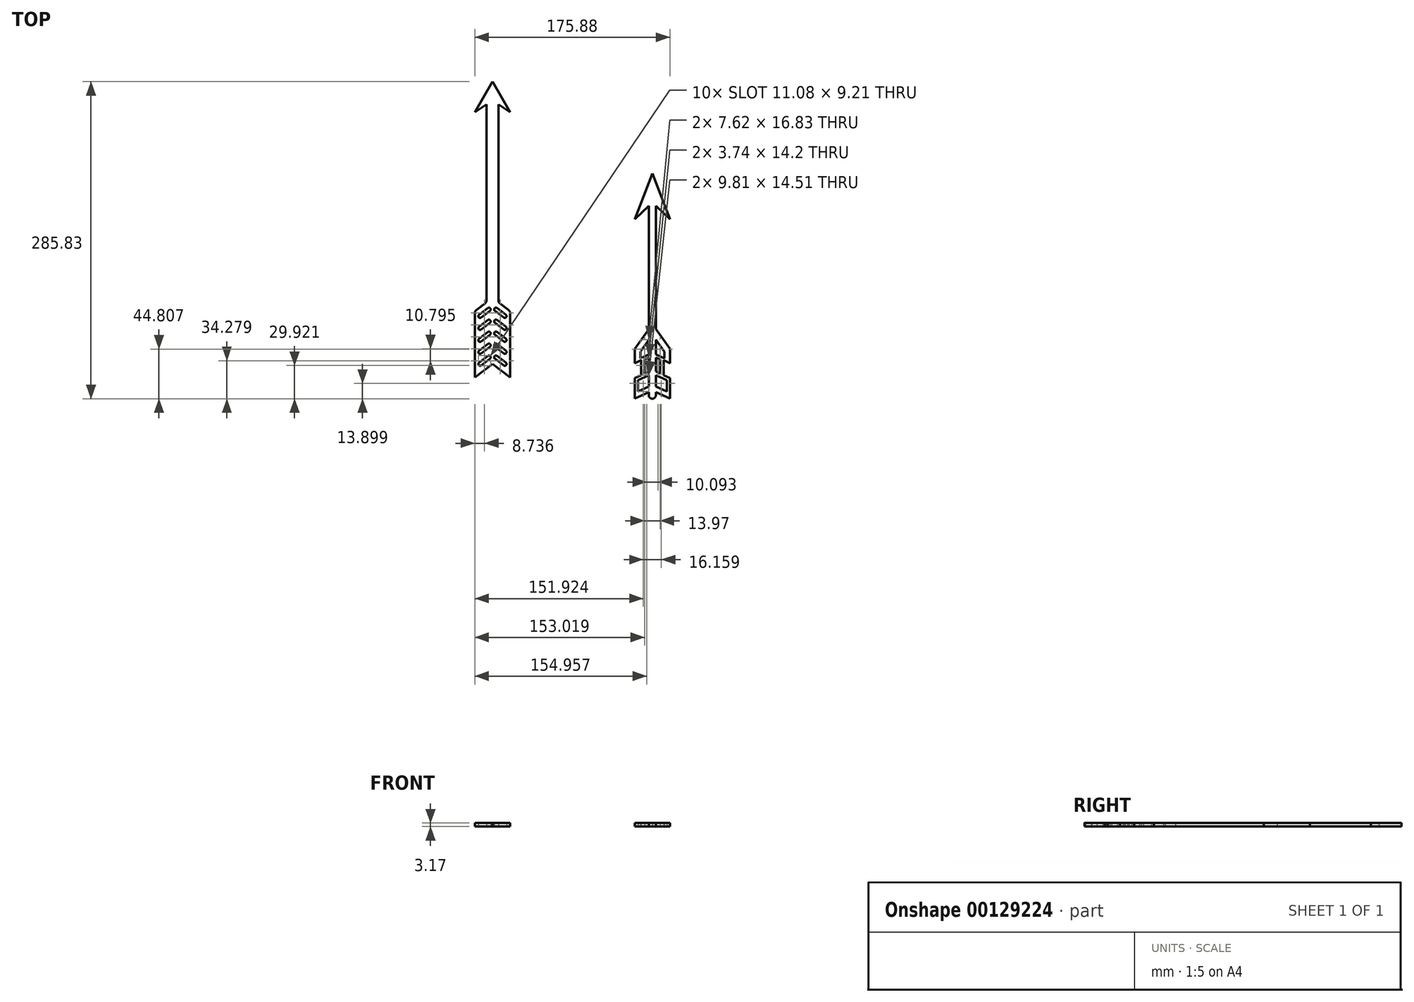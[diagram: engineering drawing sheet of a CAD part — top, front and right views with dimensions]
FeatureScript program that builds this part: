
annotation { "Feature Type Name" : "Feature", "Feature Type Description" : "" }
export const myFeature = defineFeature(function(context is Context, id is Id, definition is map)
    precondition{}
    {
        {
            var Q0;
            Q0=qCreatedBy(makeId("Top.planeOp"),FACE);
            var sketch = newSketch(context, id + "F0", { "sketchPlane" : qUnion([Q0])});
            skLineSegment(sketch, "E0", {"start": v(0, 149.15) * mm, "end": v(-15.88, 121.63) * mm});
            skLineSegment(sketch, "E1", {"start": v(5.4, 128.72) * mm, "end": v(-5.4, 128.72) * mm});
            skPoint(sketch, "E2", {"position": v(0, 128.72) * mm});
            skLineSegment(sketch, "E3", {"start": v(-5.4, 128.72) * mm, "end": v(-15.87, 121.63) * mm});
            skLineSegment(sketch, "E4", {"start": v(-5.4, 128.72) * mm, "end": v(-5.4, -48.22) * mm});
            skLineSegment(sketch, "E5", {"start": v(-6.65, -50.75) * mm, "end": v(-14.63, -56.84) * mm});
            skLineSegment(sketch, "E6", {"start": v(-15.88, -59.36) * mm, "end": v(-15.88, -117.55) * mm});
            skLineSegment(sketch, "E7", {"start": v(-15.87, -117.55) * mm, "end": v(0, -105.43) * mm});
            skLineSegment(sketch, "E8", {"start": v(0, 149.15) * mm, "end": v(0, -105.43) * mm, "construction": true});
            skLineSegment(sketch, "E9", {"start": v(-3.17, -99.37) * mm, "end": v(-11.11, -105.43) * mm});
            skLineSegment(sketch, "E10.0.1.0", {"start": v(-3.17, -88.58) * mm, "end": v(-11.11, -94.63) * mm});
            skLineSegment(sketch, "E10.0.2.0", {"start": v(-3.17, -77.78) * mm, "end": v(-11.11, -83.84) * mm});
            skLineSegment(sketch, "E10.0.3.0", {"start": v(-3.17, -66.99) * mm, "end": v(-11.11, -73.04) * mm});
            skLineSegment(sketch, "E10.0.4.0", {"start": v(-3.17, -56.2) * mm, "end": v(-11.11, -62.25) * mm});
            skLineSegment(sketch, "E10.direction1", {"start": v(-11.11, -105.43) * mm, "end": v(14.87, -105.43) * mm, "construction": true});
            skLineSegment(sketch, "E10.direction2", {"start": v(-11.11, -105.43) * mm, "end": v(-11.11, -94.63) * mm, "construction": true});
            skArc(sketch, "E11.0.startCap", {"start": v(-4.14, -98.1) * mm, "mid": v(-1.91, -98.4) * mm, "end": v(-2.21, -100.63) * mm});
            skArc(sketch, "E11.0.endCap", {"start": v(-10.15, -106.7) * mm, "mid": v(-12.37, -106.4) * mm, "end": v(-12.08, -104.17) * mm});
            skLineSegment(sketch, "E11.0.left", {"start": v(-2.21, -100.63) * mm, "end": v(-10.15, -106.7) * mm});
            skLineSegment(sketch, "E11.0.right", {"start": v(-4.14, -98.1) * mm, "end": v(-12.08, -104.17) * mm});
            skArc(sketch, "E11.1.startCap", {"start": v(-4.14, -87.31) * mm, "mid": v(-1.91, -87.61) * mm, "end": v(-2.21, -89.84) * mm});
            skArc(sketch, "E11.1.endCap", {"start": v(-10.15, -95.9) * mm, "mid": v(-12.37, -95.6) * mm, "end": v(-12.08, -93.37) * mm});
            skLineSegment(sketch, "E11.1.left", {"start": v(-2.21, -89.84) * mm, "end": v(-10.15, -95.9) * mm});
            skLineSegment(sketch, "E11.1.right", {"start": v(-4.14, -87.31) * mm, "end": v(-12.08, -93.37) * mm});
            skArc(sketch, "E11.2.startCap", {"start": v(-4.14, -76.52) * mm, "mid": v(-1.91, -76.82) * mm, "end": v(-2.21, -79.04) * mm});
            skArc(sketch, "E11.2.endCap", {"start": v(-10.15, -85.1) * mm, "mid": v(-12.37, -84.8) * mm, "end": v(-12.08, -82.58) * mm});
            skLineSegment(sketch, "E11.2.left", {"start": v(-2.21, -79.04) * mm, "end": v(-10.15, -85.1) * mm});
            skLineSegment(sketch, "E11.2.right", {"start": v(-4.14, -76.52) * mm, "end": v(-12.08, -82.58) * mm});
            skArc(sketch, "E11.3.startCap", {"start": v(-4.14, -65.72) * mm, "mid": v(-1.91, -66.02) * mm, "end": v(-2.21, -68.25) * mm});
            skArc(sketch, "E11.3.endCap", {"start": v(-10.15, -74.3) * mm, "mid": v(-12.37, -74) * mm, "end": v(-12.08, -71.78) * mm});
            skLineSegment(sketch, "E11.3.left", {"start": v(-2.21, -68.25) * mm, "end": v(-10.15, -74.3) * mm});
            skLineSegment(sketch, "E11.3.right", {"start": v(-4.14, -65.72) * mm, "end": v(-12.08, -71.78) * mm});
            skArc(sketch, "E11.4.startCap", {"start": v(-4.14, -54.93) * mm, "mid": v(-1.91, -55.23) * mm, "end": v(-2.21, -57.45) * mm});
            skArc(sketch, "E11.4.endCap", {"start": v(-10.15, -63.51) * mm, "mid": v(-12.37, -63.21) * mm, "end": v(-12.08, -60.99) * mm});
            skLineSegment(sketch, "E11.4.left", {"start": v(-2.21, -57.45) * mm, "end": v(-10.15, -63.51) * mm});
            skLineSegment(sketch, "E11.4.right", {"start": v(-4.14, -54.93) * mm, "end": v(-12.08, -60.99) * mm});
            skPoint(sketch, "E12.visualSharp", {"position": v(-5.4, -49.8) * mm});
            skArc(sketch, "E12.filletArc", {"start": v(-6.65, -50.75) * mm, "mid": v(-5.73, -49.63) * mm, "end": v(-5.4, -48.22) * mm});
            skPoint(sketch, "E13.visualSharp", {"position": v(-15.87, -57.8) * mm});
            skArc(sketch, "E13.filletArc", {"start": v(-14.63, -56.84) * mm, "mid": v(-15.55, -57.95) * mm, "end": v(-15.88, -59.36) * mm});
            skArc(sketch, "E14.MirrorCS", {"start": v(10.15, -85.1) * mm, "mid": v(12.37, -84.8) * mm, "end": v(12.08, -82.58) * mm});
            skLineSegment(sketch, "E15.MirrorCS", {"start": v(4.14, -65.72) * mm, "end": v(12.08, -71.78) * mm});
            skArc(sketch, "E16.MirrorCS", {"start": v(10.15, -74.3) * mm, "mid": v(12.37, -74) * mm, "end": v(12.08, -71.78) * mm});
            skArc(sketch, "E17.MirrorCS", {"start": v(10.15, -63.51) * mm, "mid": v(12.37, -63.21) * mm, "end": v(12.08, -60.99) * mm});
            skLineSegment(sketch, "E18.MirrorCS", {"start": v(3.18, -56.2) * mm, "end": v(11.11, -62.25) * mm});
            skLineSegment(sketch, "E19.MirrorCS", {"start": v(4.14, -76.52) * mm, "end": v(12.08, -82.58) * mm});
            skLineSegment(sketch, "E20.MirrorCS", {"start": v(4.14, -98.1) * mm, "end": v(12.08, -104.17) * mm});
            skArc(sketch, "E21.MirrorCS", {"start": v(4.14, -54.93) * mm, "mid": v(1.91, -55.23) * mm, "end": v(2.21, -57.45) * mm});
            skLineSegment(sketch, "E22.MirrorCS", {"start": v(4.14, -87.31) * mm, "end": v(12.08, -93.37) * mm});
            skLineSegment(sketch, "E23.MirrorCS", {"start": v(2.21, -79.04) * mm, "end": v(10.15, -85.1) * mm});
            skLineSegment(sketch, "E24.MirrorCS", {"start": v(2.21, -57.45) * mm, "end": v(10.15, -63.51) * mm});
            skLineSegment(sketch, "E25.MirrorCS", {"start": v(2.21, -100.63) * mm, "end": v(10.15, -106.7) * mm});
            skLineSegment(sketch, "E26.MirrorCS", {"start": v(2.21, -89.84) * mm, "end": v(10.15, -95.9) * mm});
            skArc(sketch, "E27.MirrorCS", {"start": v(10.15, -106.7) * mm, "mid": v(12.37, -106.4) * mm, "end": v(12.08, -104.17) * mm});
            skLineSegment(sketch, "E28.MirrorCS", {"start": v(2.21, -68.25) * mm, "end": v(10.15, -74.3) * mm});
            skArc(sketch, "E29.MirrorCS", {"start": v(14.63, -56.84) * mm, "mid": v(15.55, -57.95) * mm, "end": v(15.88, -59.36) * mm});
            skArc(sketch, "E30.MirrorCS", {"start": v(10.15, -95.9) * mm, "mid": v(12.37, -95.6) * mm, "end": v(12.08, -93.37) * mm});
            skArc(sketch, "E31.MirrorCS", {"start": v(4.14, -76.52) * mm, "mid": v(1.91, -76.82) * mm, "end": v(2.21, -79.04) * mm});
            skArc(sketch, "E32.MirrorCS", {"start": v(4.14, -65.72) * mm, "mid": v(1.91, -66.02) * mm, "end": v(2.21, -68.25) * mm});
            skLineSegment(sketch, "E33.MirrorCS", {"start": v(3.18, -66.99) * mm, "end": v(11.11, -73.04) * mm});
            skLineSegment(sketch, "E34.MirrorCS", {"start": v(3.18, -77.78) * mm, "end": v(11.11, -83.84) * mm});
            skLineSegment(sketch, "E35.MirrorCS", {"start": v(3.18, -88.58) * mm, "end": v(11.11, -94.63) * mm});
            skLineSegment(sketch, "E36.MirrorCS", {"start": v(3.18, -99.37) * mm, "end": v(11.11, -105.43) * mm});
            skArc(sketch, "E37.MirrorCS", {"start": v(4.14, -98.1) * mm, "mid": v(1.91, -98.4) * mm, "end": v(2.21, -100.63) * mm});
            skLineSegment(sketch, "E38.MirrorCS", {"start": v(11.11, -105.43) * mm, "end": v(-14.87, -105.43) * mm, "construction": true});
            skLineSegment(sketch, "E39.MirrorCS", {"start": v(11.11, -105.43) * mm, "end": v(11.11, -94.63) * mm, "construction": true});
            skArc(sketch, "E40.MirrorCS", {"start": v(4.14, -87.31) * mm, "mid": v(1.91, -87.61) * mm, "end": v(2.21, -89.84) * mm});
            skLineSegment(sketch, "E41.MirrorCS", {"start": v(4.14, -54.93) * mm, "end": v(12.08, -60.99) * mm});
            skLineSegment(sketch, "E42.MirrorCS", {"start": v(15.87, -59.36) * mm, "end": v(15.87, -117.55) * mm});
            skLineSegment(sketch, "E43.MirrorCS", {"start": v(6.65, -50.75) * mm, "end": v(14.63, -56.84) * mm});
            skArc(sketch, "E44.MirrorCS", {"start": v(6.65, -50.75) * mm, "mid": v(5.73, -49.63) * mm, "end": v(5.4, -48.22) * mm});
            skLineSegment(sketch, "E45.MirrorCS", {"start": v(15.87, -117.55) * mm, "end": v(0, -105.43) * mm});
            skLineSegment(sketch, "E46.MirrorCS", {"start": v(5.4, 128.72) * mm, "end": v(15.87, 121.63) * mm});
            skPoint(sketch, "E47.MirrorP", {"position": v(5.4, -49.8) * mm});
            skPoint(sketch, "E48.MirrorP", {"position": v(15.88, -57.8) * mm});
            skLineSegment(sketch, "E49.MirrorCS", {"start": v(5.4, 128.72) * mm, "end": v(5.4, -48.22) * mm});
            skLineSegment(sketch, "E50.MirrorCS", {"start": v(0, 149.15) * mm, "end": v(15.88, 121.63) * mm});
            skSolve(sketch);
        }
        {
            var Q0;
            {var subQ0=sQuery(id+"F0.wireOp",EDGE,"E4");Q0=makeQuery(id+"F0.imprint","IMPRINT",FACE,{"disambiguationData":[TD([[makeQuery(id+"F0.imprint","IMPRINT",EDGE,{"derivedFrom":subQ0}),1.0]])]});}
            var Q1;
            {var subQ0=sQuery(id+"F0.wireOp",EDGE,"E0");Q1=makeQuery(id+"F0.imprint","IMPRINT",FACE,{"disambiguationData":[TD([[makeQuery(id+"F0.imprint","IMPRINT",EDGE,{"derivedFrom":subQ0}),1.0]])]});}
            var Q2;
            {var subQ0=sQuery(id+"F0.wireOp",EDGE,"E46.MirrorCS");Q2=makeQuery(id+"F0.imprint","IMPRINT",FACE,{"disambiguationData":[TD([[makeQuery(id+"F0.imprint","IMPRINT",EDGE,{"derivedFrom":subQ0}),1.0]])]});}
            var Q3;
            Q3=makeQuery(id+"F0.imprint","IMPRINT",FACE,{"disambiguationData":[TD([[makeQuery(id+"F0.imprint","IMPRINT",EDGE,{"derivedFrom":sQuery(id+"F0.wireOp",EDGE,"E14.MirrorCS")}),-1.0]])]});
            extrude(context, id + "F1", {"entities" : qUnion([Q0, Q1, Q2, Q3]), "depth" : 3.17 * mm});
        }
        {
            var Q0;
            Q0=qCreatedBy(makeId("Top.planeOp"),FACE);
            var sketch = newSketch(context, id + "F2", { "sketchPlane" : qUnion([Q0])});
            skLineSegment(sketch, "E51", {"start": v(140.95, 37.12) * mm, "end": v(140.95, -73.97) * mm});
            skLineSegment(sketch, "E52", {"start": v(140.95, -73.97) * mm, "end": v(128.25, -91.78) * mm});
            skLineSegment(sketch, "E53", {"start": v(128.25, -91.78) * mm, "end": v(128.25, -104.58) * mm});
            skLineSegment(sketch, "E54", {"start": v(128.25, -104.58) * mm, "end": v(134.03, -101.95) * mm});
            skLineSegment(sketch, "E55", {"start": v(134.03, -101.95) * mm, "end": v(134.03, -115.48) * mm});
            skLineSegment(sketch, "E56", {"start": v(134.03, -115.48) * mm, "end": v(128.25, -118.1) * mm});
            skLineSegment(sketch, "E57", {"start": v(128.25, -118.1) * mm, "end": v(128.25, -136.39) * mm});
            skLineSegment(sketch, "E58", {"start": v(128.25, -136.39) * mm, "end": v(140.95, -130.62) * mm});
            skLineSegment(sketch, "E59", {"start": v(140.95, -130.62) * mm, "end": v(140.95, -133.5) * mm});
            skPoint(sketch, "E59.endSnap0", {"position": v(134.6, -133.5) * mm});
            skArc(sketch, "E60", {"start": v(140.95, -133.5) * mm, "mid": v(141.88, -135.75) * mm, "end": v(144.12, -136.68) * mm});
            skLineSegment(sketch, "E61", {"start": v(140.95, 37.12) * mm, "end": v(128.25, 25.06) * mm});
            skLineSegment(sketch, "E62", {"start": v(128.25, 25.06) * mm, "end": v(144.12, 66.52) * mm});
            skLineSegment(sketch, "E63", {"start": v(144.12, -136.68) * mm, "end": v(144.12, 66.52) * mm, "construction": true});
            skPoint(sketch, "E64.orphan", {"position": v(147.3, -133.5) * mm});
            skLineSegment(sketch, "E65.MirrorCS", {"start": v(154.22, -115.48) * mm, "end": v(160, -118.1) * mm});
            skLineSegment(sketch, "E66.MirrorCS", {"start": v(160, -104.58) * mm, "end": v(154.22, -101.95) * mm});
            skLineSegment(sketch, "E67.MirrorCS", {"start": v(154.22, -101.95) * mm, "end": v(154.22, -115.48) * mm});
            skLineSegment(sketch, "E68.MirrorCS", {"start": v(147.3, -130.62) * mm, "end": v(147.3, -133.5) * mm});
            skArc(sketch, "E69.MirrorCS", {"start": v(147.3, -133.5) * mm, "mid": v(146.37, -135.75) * mm, "end": v(144.12, -136.68) * mm});
            skLineSegment(sketch, "E70.MirrorCS", {"start": v(160, -136.39) * mm, "end": v(147.3, -130.62) * mm});
            skLineSegment(sketch, "E71.MirrorCS", {"start": v(160, -118.1) * mm, "end": v(160, -136.39) * mm});
            skLineSegment(sketch, "E72.MirrorCS", {"start": v(160, -91.78) * mm, "end": v(160, -104.58) * mm});
            skLineSegment(sketch, "E73.MirrorCS", {"start": v(147.3, -73.97) * mm, "end": v(160, -91.78) * mm});
            skLineSegment(sketch, "E74.MirrorCS", {"start": v(147.3, 37.12) * mm, "end": v(147.3, -73.97) * mm});
            skLineSegment(sketch, "E75.MirrorCS", {"start": v(160, 25.06) * mm, "end": v(144.12, 66.52) * mm});
            skLineSegment(sketch, "E76.MirrorCS", {"start": v(147.3, 37.12) * mm, "end": v(160, 25.06) * mm});
            skLineSegment(sketch, "E77", {"start": v(140.95, -83.46) * mm, "end": v(133.33, -94.14) * mm});
            skLineSegment(sketch, "E78", {"start": v(133.33, -94.14) * mm, "end": v(133.33, -100.29) * mm});
            skLineSegment(sketch, "E79", {"start": v(133.33, -100.29) * mm, "end": v(140.95, -96.83) * mm});
            skLineSegment(sketch, "E80", {"start": v(140.95, -96.83) * mm, "end": v(140.95, -83.46) * mm});
            skLineSegment(sketch, "E81", {"start": v(140.95, -115.53) * mm, "end": v(131.14, -119.98) * mm});
            skPoint(sketch, "E81.endSnap0", {"position": v(131.14, -116.8) * mm});
            skLineSegment(sketch, "E82", {"start": v(131.14, -119.98) * mm, "end": v(131.14, -130.04) * mm});
            skLineSegment(sketch, "E83", {"start": v(131.14, -130.04) * mm, "end": v(140.95, -125.58) * mm});
            skLineSegment(sketch, "E84", {"start": v(140.95, -125.58) * mm, "end": v(140.95, -115.53) * mm});
            skLineSegment(sketch, "E85", {"start": v(137.2, -101.36) * mm, "end": v(137.2, -113.86) * mm});
            skLineSegment(sketch, "E86", {"start": v(137.2, -113.86) * mm, "end": v(140.95, -112.16) * mm});
            skLineSegment(sketch, "E87", {"start": v(140.95, -112.16) * mm, "end": v(140.95, -99.66) * mm});
            skLineSegment(sketch, "E88", {"start": v(140.95, -99.66) * mm, "end": v(137.2, -101.36) * mm});
            skLineSegment(sketch, "E89.MirrorCS", {"start": v(147.3, -96.83) * mm, "end": v(147.3, -83.46) * mm});
            skLineSegment(sketch, "E90.MirrorCS", {"start": v(147.3, -83.46) * mm, "end": v(154.92, -94.14) * mm});
            skLineSegment(sketch, "E91.MirrorCS", {"start": v(154.92, -100.29) * mm, "end": v(147.3, -96.83) * mm});
            skLineSegment(sketch, "E92.MirrorCS", {"start": v(154.92, -94.14) * mm, "end": v(154.92, -100.29) * mm});
            skLineSegment(sketch, "E93.MirrorCS", {"start": v(147.3, -112.16) * mm, "end": v(147.3, -99.66) * mm});
            skLineSegment(sketch, "E94.MirrorCS", {"start": v(147.3, -99.66) * mm, "end": v(151.04, -101.36) * mm});
            skLineSegment(sketch, "E95.MirrorCS", {"start": v(151.04, -101.36) * mm, "end": v(151.04, -113.86) * mm});
            skLineSegment(sketch, "E96.MirrorCS", {"start": v(151.04, -113.86) * mm, "end": v(147.3, -112.16) * mm});
            skLineSegment(sketch, "E97.MirrorCS", {"start": v(157.1, -130.04) * mm, "end": v(147.3, -125.58) * mm});
            skLineSegment(sketch, "E98.MirrorCS", {"start": v(147.3, -125.58) * mm, "end": v(147.3, -115.53) * mm});
            skLineSegment(sketch, "E99.MirrorCS", {"start": v(157.1, -119.98) * mm, "end": v(157.1, -130.04) * mm});
            skLineSegment(sketch, "E100.MirrorCS", {"start": v(147.3, -115.53) * mm, "end": v(157.1, -119.98) * mm});
            skLineSegment(sketch, "E101", {"start": v(131.14, -130.04) * mm, "end": v(131.14, -135.07) * mm, "construction": true});
            skLineSegment(sketch, "E102", {"start": v(139.08, -116.38) * mm, "end": v(139.08, -113.86) * mm, "construction": true});
            skLineSegment(sketch, "E103", {"start": v(138.5, -100.77) * mm, "end": v(138.5, -97.94) * mm, "construction": true});
            skLineSegment(sketch, "E104", {"start": v(133.33, -94.14) * mm, "end": v(133.33, -84.66) * mm, "construction": true});
            skSolve(sketch);
        }
        {
            var Q0;
            Q0=makeQuery(id+"F2.imprint","IMPRINT",FACE,{"disambiguationData":[TD([[makeQuery(id+"F2.imprint","IMPRINT",EDGE,{"derivedFrom":sQuery(id+"F2.wireOp",EDGE,"E51")}),1.0]])]});
            extrude(context, id + "F3", {"entities" : qUnion([Q0]), "depth" : 3.17 * mm});
        }
    });
